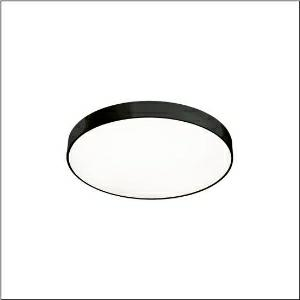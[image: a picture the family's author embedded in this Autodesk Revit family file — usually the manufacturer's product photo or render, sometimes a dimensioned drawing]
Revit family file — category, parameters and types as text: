
# Revit family: round_21_m_51mr36fd0421b
name_source: partatom
category: Lighting Fixtures
units: mm (PartAtom-declared; Revit-internal decimal feet)

## family parameters
Cut with Voids When Loaded = No
Host = Face
Light Source = No
Part Type = Normal
Room Calculation Point = No
Round Connector Dimension = Use Diameter
Shared = No

## types (1)
- Round 21 M (1 x LED, 7810 lm, 54.9 W, 4000K)
    Apparent Load = 55 VA
    CIE Flux Codes = 49 80 96 100 100
    Color Rendering = 80
    Color Temperature = 4000K
    Default Elevation = 1800 mm
    Description = Round 21 M, wall and ceiling luminaire, primary optical cover: cover, of PMMA, opal, light emission: direct distribution, primary light characteristic: symmetric, installation type: surface-mounted, suspended mounting, LED, rated luminous flux: 7.810lm, luminous efficacy: 142lm/W, light colour: 840, colour temperature: 4000K, control gear: DALI 2, with terminal, 5-pole, mains connection: 230V, AC, 50/60Hz, rated input power: 55W, housing, of aluminium, coated, black, diameter: 600mm, height: 62mm, protection rating (complete): IP40, insulation class (complete): insulation class I (protective earthing), certification: CE, impact resistance: IK04, permissible operating ambient temperature: -10..+35°C, packaging unit: 1 piece
    Height = 87 mm
    Lamp = 1 x LED
    Lamp Light Flux = 7810 lm
    Lamp Power = 54.9 W
    Lamp count = 1
    Length = 600 mm
    Luminous efficacy = 142 lm/W
    Manufacturer = Siteco
    ModVariant = No
    Model = 51MR36FD0421B
    Mounting Place = Ceiling
    Mounting Type = Surface mounted
    Number of Poles = 1
    OnlyDefault = Yes
    Power Factor = 1
    Product Name = Round 21 M
    Product group = wall and ceiling luminaire | ceiling mounted
    ProductGroupID = 305
    Protection Class = Protection class I
    Protection Degree = IP 40
    RLX_Detail_Level = 1
    RLX_Emergency_Light_Flux = 0 lm
    RLX_Emergency_Type = 0
    RLX_Emergency_Type_DB = No
    RlxData = <blob elided: 17745 chars, md5=d3f1d63b>
    Socket = socket
    Standby Power = 0 W
    System Light Flux = 7810 lm
    System Power = 55 W
    Type Comments = Product without accessories
    Type Image = l_1258332.jpg
    URL = http://relux.com
    VarID = ---
    Voltage = 0 V
    Weight = 0.00 kg
    Width = 0 mm  [stored 0 ft]

note: [stored X ft] marks values corroborated as IEEE doubles in the binary element streams (Revit-internal decimal feet)

## geometry (parser evidence)
native form markers: Blend x4, Sweep x11
no freeform markers — native parametric forms only
